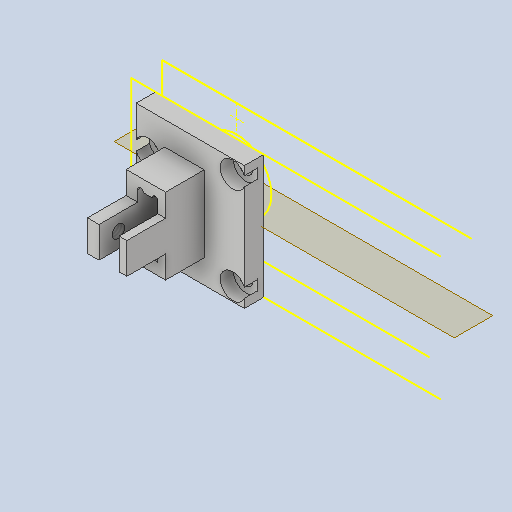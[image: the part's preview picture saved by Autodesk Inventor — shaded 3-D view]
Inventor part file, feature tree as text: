
AUTODESK INVENTOR PART (.ipt)
format: ipt  version: 2025 (Build 290162000, 162)  size: 442,880 bytes
history: native  units: mm
features: extrude x4, other x3, hole x2, plane x1
ambient origin geometry x8: Origin, YZ Plane, XZ Plane, XY Plane, X Axis, Y Axis, Z Axis, Center Point
bodies: Volumenkörper2 (feature_tree), Volumenkörper1 (feature_tree)
feature tree (10):
  other  "Halterung_Optik.ipt"
  extrude  "Extrusion1"  Depth=10.0mm
  hole  "Bohrung1"  [1 undecoded]
  extrude  "Extrusion2"  Depth=3.0mm
  extrude  "Extrusion4"  Depth=5.0mm TaperAngle=0.0deg
  extrude  "Extrusion3"  Depth=2.6mm
  hole  "Bohrung3"  [1 undecoded]
  other  "Volumenkörper1::Halterung_Optik.ipt"
  other  "Bezeichnung1"
  plane  "Arbeitsebene1"
note: 2 required parameter values undecoded (feature->parameter linkage not recoverable at this tier; creation-order binding heuristic only, values carry confidence <= 0.55)
